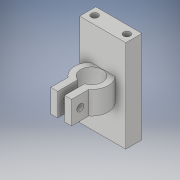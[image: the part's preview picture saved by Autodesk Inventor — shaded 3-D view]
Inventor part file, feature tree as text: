
AUTODESK INVENTOR PART (.ipt)
format: ipt  version: 2019 (Build 230136000, 136)  size: 144,896 bytes
history: native  units: mm
features: sketch x4, extrude x2, hole x2
ambient origin geometry x8: Origin, YZ Plane, XZ Plane, XY Plane, X Axis, Y Axis, Z Axis, Center Point
bodies: Solid1 (feature_tree)
feature tree (8):
  extrude  "Extrusion1"  Depth=10.0mm TaperAngle=0.0deg
  extrude  "Extrusion2"  Depth=10.0mm
  hole  "Hole1"  [1 undecoded]
  hole  "Hole2"  [1 undecoded]
  sketch  "Sketch1"  dims[d4=14.5mm d11=10.0mm d12=0.0mm]
  sketch  "Sketch2"  dims[d13=10.0mm d14=10.0mm]
  sketch  "Sketch3"  dims[d15=7.0mm d16=20.0mm]
  sketch  "Sketch4"  dims[d17=7.0mm d18=25.0mm d19=15.0mm d20=0.0mm d21=0.0mm d24=3.0mm d27=3.0mm d28=3.0mm d29=6.0mm d30=4.0mm d31=2.0mm d32=90.0deg d33=8.0mm d34=20.594885mm d36=3.0mm d37=3.0mm d38=6.0mm d39=4.0mm d40=2.0mm d41=90.0deg d42=8.0mm d43=20.594885mm]
note: 2 required parameter values undecoded (feature->parameter linkage not recoverable at this tier; creation-order binding heuristic only, values carry confidence <= 0.55)
